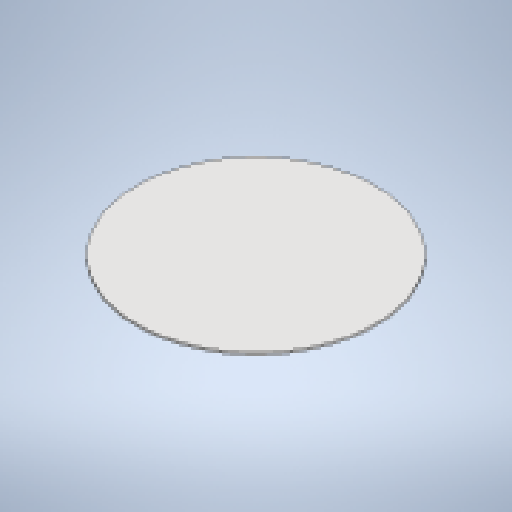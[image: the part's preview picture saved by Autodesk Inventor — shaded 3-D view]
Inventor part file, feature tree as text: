
AUTODESK INVENTOR PART (.ipt)
format: ipt  version: 2025.1 (Build 291241000, 241)  size: 107,520 bytes
history: native  units: mm
features: extrude x1, sketch x1
ambient origin geometry x8: Origin, YZ Plane, XZ Plane, XY Plane, X Axis, Y Axis, Z Axis, Center Point
bodies: 实体1 (feature_tree)
feature tree (2):
  extrude  "拉伸1"  [1 undecoded]
  sketch  "草图1"  dims[d0=10.0mm d1=0.0mm]
note: 1 required parameter value undecoded (feature->parameter linkage not recoverable at this tier; creation-order binding heuristic only, values carry confidence <= 0.55)
